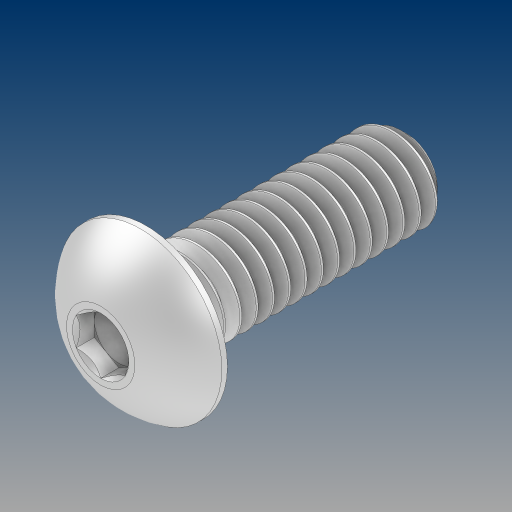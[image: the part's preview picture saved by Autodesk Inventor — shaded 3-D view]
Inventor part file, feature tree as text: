
AUTODESK INVENTOR PART (.ipt)
format: ipt  version: 2024.3 (Build 283343000, 343)  size: 607,232 bytes
history: native  units: in
note: dims shown in document units (in); Inventor stores cm internally (conversion verified against a paired STEP export)
features: revolve x1
ambient origin geometry x8: Origin, YZ Plane, XZ Plane, XY Plane, X Axis, Y Axis, Z Axis, Center Point
bodies: Solid1 (feature_tree)
feature tree (1):
  revolve  "Revolve2"  [1 undecoded]
note: 1 required parameter value undecoded (feature->parameter linkage not recoverable at this tier; creation-order binding heuristic only, values carry confidence <= 0.55)
